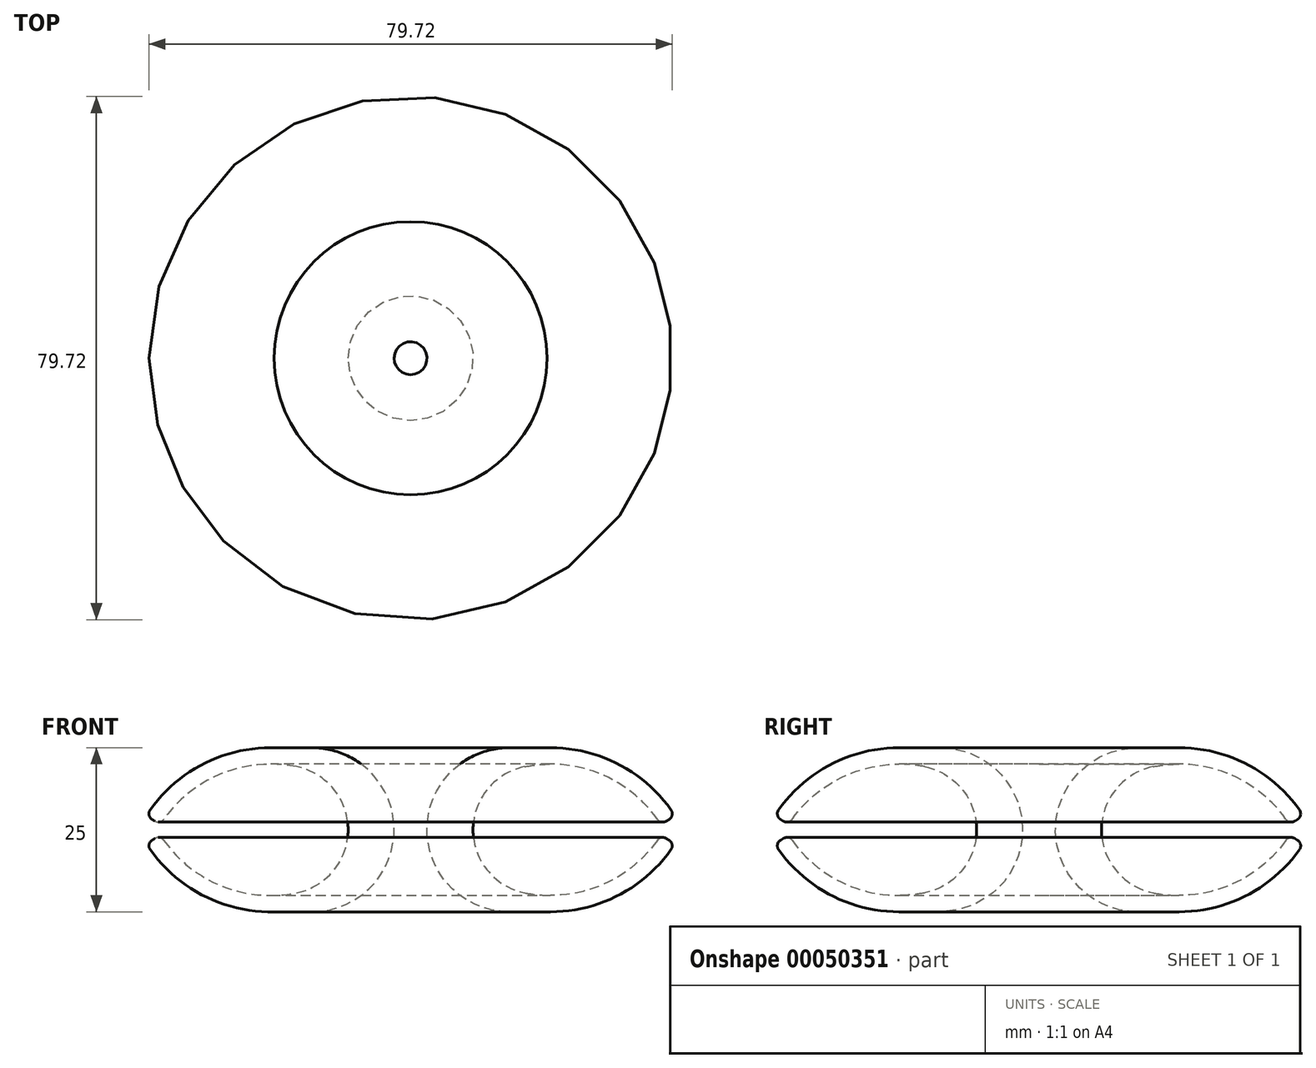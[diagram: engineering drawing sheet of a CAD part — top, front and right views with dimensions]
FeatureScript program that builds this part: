
annotation { "Feature Type Name" : "Feature", "Feature Type Description" : "" }
export const myFeature = defineFeature(function(context is Context, id is Id, definition is map)
    precondition{}
    {
        {
            var Q0;
            Q0=qCreatedBy(makeId("Front.planeOp"),FACE);
            var sketch = newSketch(context, id + "F0", { "sketchPlane" : qUnion([Q0])});
            skLineSegment(sketch, "E0", {"start": v(0, 0) * mm, "end": v(0, 29.97) * mm, "construction": true});
            skArc(sketch, "E1", {"start": v(-13.38, 9.6) * mm, "mid": v(-24.68, 8.6) * mm, "end": v(-33.62, 1.6) * mm});
            skLineSegment(sketch, "E2", {"start": v(0, 0) * mm, "end": v(-34.64, 0) * mm, "construction": true});
            skLineSegment(sketch, "E3", {"start": v(4, 0) * mm, "end": v(4, 14.99) * mm, "construction": true});
            skPoint(sketch, "E3.endSnap0", {"position": v(0, 14.99) * mm});
            skPoint(sketch, "E4.visualSharp", {"position": v(-34.64, 0) * mm});
            skLineSegment(sketch, "E5", {"start": v(-16.8, 12.5) * mm, "end": v(-11, 12.5) * mm});
            skArc(sketch, "E6.trimOffspring", {"start": v(-16.8, 12.5) * mm, "mid": v(-27.41, 10.1) * mm, "end": v(-35.67, 3.02) * mm});
            skPoint(sketch, "E7.MirrorP", {"position": v(0, -14.99) * mm});
            skLineSegment(sketch, "E8.MirrorCS", {"start": v(4, 0) * mm, "end": v(4, -14.99) * mm, "construction": true});
            skArc(sketch, "E9.MirrorCS", {"start": v(-13.38, -9.6) * mm, "mid": v(-24.68, -8.6) * mm, "end": v(-33.62, -1.6) * mm});
            skArc(sketch, "E10.MirrorCS", {"start": v(-16.8, -12.5) * mm, "mid": v(-27.41, -10.1) * mm, "end": v(-35.67, -3.02) * mm});
            skLineSegment(sketch, "E11.MirrorCS", {"start": v(-16.8, -12.5) * mm, "end": v(-11, -12.5) * mm});
            skPoint(sketch, "E12.visualSharp", {"position": v(0, 0) * mm});
            skArc(sketch, "E12.filletArc", {"start": v(-13.38, -9.6) * mm, "mid": v(-5.51, 0) * mm, "end": v(-13.38, 9.6) * mm});
            skArc(sketch, "E13", {"start": v(-11, -12.5) * mm, "mid": v(1.5, 0) * mm, "end": v(-11, 12.5) * mm});
            skPoint(sketch, "E14.orphan", {"position": v(4, 12.5) * mm});
            skPoint(sketch, "E15.orphan", {"position": v(4, -12.5) * mm});
            skLineSegment(sketch, "E16", {"start": v(-35.39, 1.6) * mm, "end": v(-34.96, 1.33) * mm});
            skLineSegment(sketch, "E17", {"start": v(-35.39, -1.6) * mm, "end": v(-34.96, -1.33) * mm});
            skPoint(sketch, "E18.visualSharp", {"position": v(-34.15, 0.81) * mm});
            skArc(sketch, "E18.filletArc", {"start": v(-34.96, 1.33) * mm, "mid": v(-34.24, 1.2) * mm, "end": v(-33.62, 1.6) * mm});
            skPoint(sketch, "E19.visualSharp", {"position": v(-34.15, -0.81) * mm});
            skArc(sketch, "E19.filletArc", {"start": v(-33.62, -1.6) * mm, "mid": v(-34.24, -1.2) * mm, "end": v(-34.96, -1.33) * mm});
            skPoint(sketch, "E20.visualSharp", {"position": v(-36.26, 2.14) * mm});
            skArc(sketch, "E20.filletArc", {"start": v(-35.67, 3.02) * mm, "mid": v(-35.84, 2.25) * mm, "end": v(-35.39, 1.6) * mm});
            skPoint(sketch, "E21.visualSharp", {"position": v(-36.26, -2.14) * mm});
            skArc(sketch, "E21.filletArc", {"start": v(-35.39, -1.6) * mm, "mid": v(-35.84, -2.25) * mm, "end": v(-35.67, -3.02) * mm});
            skSolve(sketch);
        }
        {
            var Q0;
            Q0=makeQuery(id+"F0.imprint","IMPRINT",FACE,{"disambiguationData":[TD([[makeQuery(id+"F0.imprint","IMPRINT",EDGE,{"derivedFrom":sQuery(id+"F0.wireOp",EDGE,"E1")}),-1.0]])]});
            var Q1;
            Q1=sQuery(id+"F0.wireOp",EDGE,"E3");
            revolve(context, id + "F1", {"entities" : qUnion([Q0]), "axis" : qUnion([Q1]), "revolveType" : RevolveType.FULL});
        }
    });
